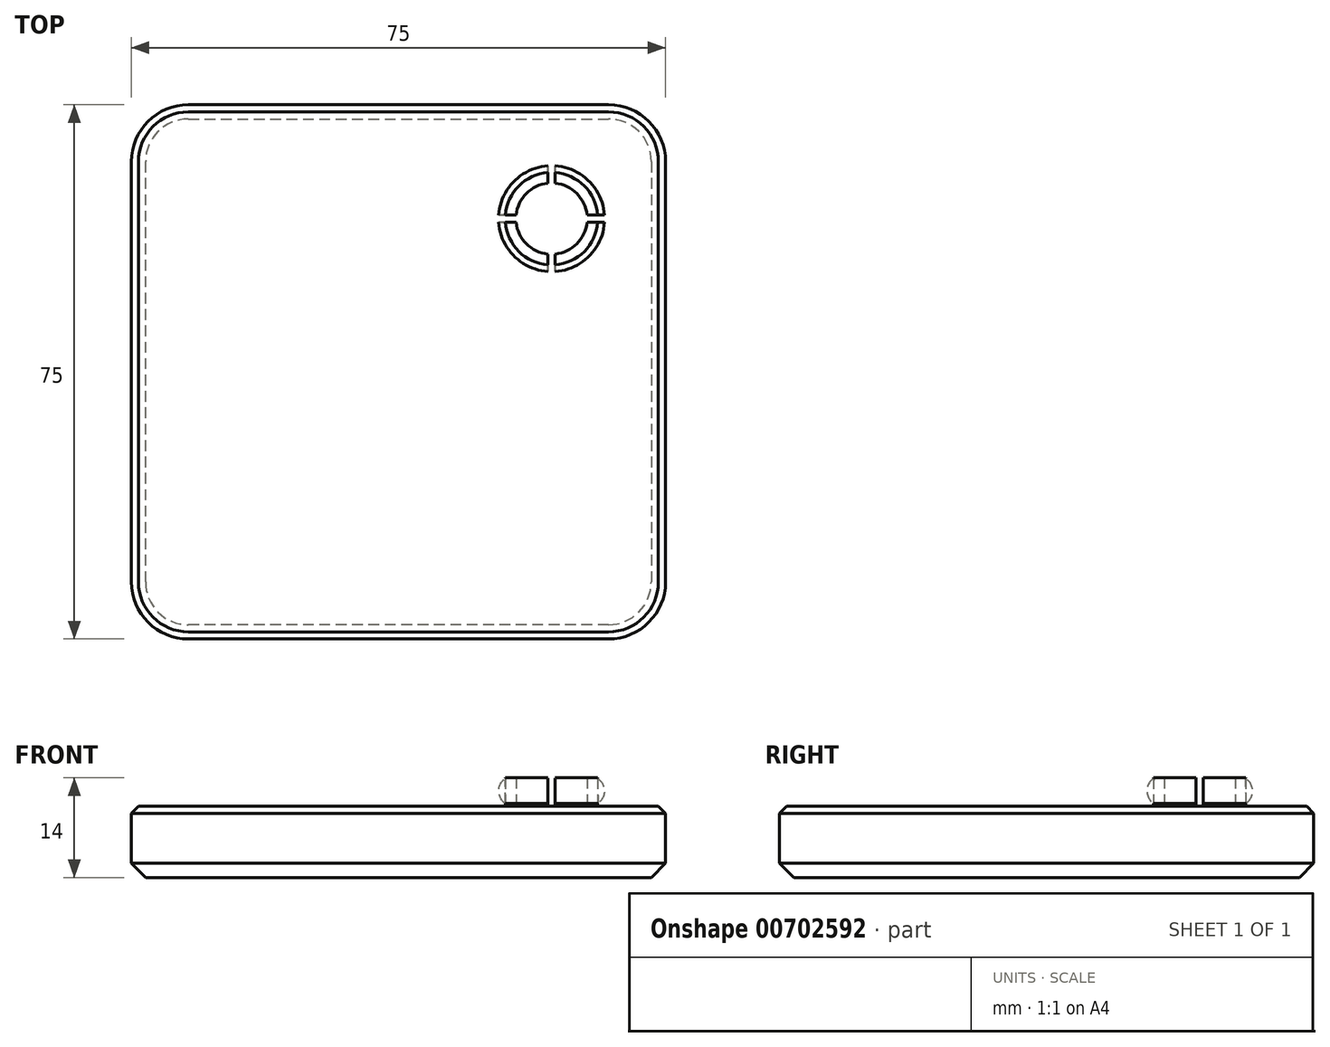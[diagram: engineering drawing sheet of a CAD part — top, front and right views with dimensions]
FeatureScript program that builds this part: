
annotation { "Feature Type Name" : "Feature", "Feature Type Description" : "" }
export const myFeature = defineFeature(function(context is Context, id is Id, definition is map)
    precondition{}
    {
        {
            var Q0;
            Q0=qCreatedBy(makeId("Top.planeOp"),FACE);
            var sketch = newSketch(context, id + "F0", { "sketchPlane" : qUnion([Q0])});
            skLineSegment(sketch, "E0.bottom", {"start": v(16, 16) * mm, "end": v(-59, 16) * mm});
            skLineSegment(sketch, "E0.top", {"start": v(16, -59) * mm, "end": v(-59, -59) * mm});
            skLineSegment(sketch, "E0.left", {"start": v(16, 16) * mm, "end": v(16, -59) * mm});
            skLineSegment(sketch, "E0.right", {"start": v(-59, 16) * mm, "end": v(-59, -59) * mm});
            skCircle(sketch, "E1", {"center": v(0, 0) * mm, "radius": 6.5 * mm});
            skCircle(sketch, "E2.0", {"center": v(0, 0) * mm, "radius": 5 * mm});
            skSolve(sketch);
        }
        {
            var Q0;
            Q0=makeQuery(id+"F0.imprint","IMPRINT",FACE,{"disambiguationData":[TD([[makeQuery(id+"F0.imprint","IMPRINT",EDGE,{"derivedFrom":sQuery(id+"F0.wireOp",EDGE,"E1")}),1.0]])]});
            var Q1;
            Q1=sQuery(id+"F0.wireOp",EDGE,"E1");
            var Q2;
            Q2=sQuery(id+"F0.wireOp",EDGE,"E2.0");
            extrude(context, id + "F1", {"entities" : qUnion([Q0]), "surfaceEntities" : qUnion([Q1, Q2]), "depth" : 4 * mm, "offsetDistance" : 25 * mm});
        }
        {
            var Q0;
            Q0=makeQuery(id+"F0.imprint","IMPRINT",FACE,{"disambiguationData":[TD([[makeQuery(id+"F0.imprint","IMPRINT",EDGE,{"derivedFrom":sQuery(id+"F0.wireOp",EDGE,"E0.bottom")}),1.0]])]});
            var Q1;
            Q1=makeQuery(id+"F0.imprint","IMPRINT",FACE,{"disambiguationData":[TD([[makeQuery(id+"F0.imprint","IMPRINT",EDGE,{"derivedFrom":sQuery(id+"F0.wireOp",EDGE,"E2.0")}),1.0]])]});
            var Q2;
            Q2=makeQuery(id+"F0.imprint","IMPRINT",FACE,{"disambiguationData":[TD([[makeQuery(id+"F0.imprint","IMPRINT",EDGE,{"derivedFrom":sQuery(id+"F0.wireOp",EDGE,"E1")}),1.0]])]});
            extrude(context, id + "F2", {"entities" : qUnion([Q0, Q1, Q2]), "operationType" : NewBodyOperationType.ADD, "oppositeDirection" : true, "depth" : 10 * mm, "offsetDistance" : 25 * mm});
        }
        {
            var Q0;
            Q0=makeQuery(id+"F2.opExtrude","SWEPT_EDGE",EDGE,{"disambiguationData":[OSD([sQuery(id+"F0.wireOp",EDGE,"E0.top"),sQuery(id+"F0.wireOp",EDGE,"E0.right")])]});
            var Q1;
            Q1=makeQuery(id+"F2.opExtrude","SWEPT_EDGE",EDGE,{"disambiguationData":[OSD([sQuery(id+"F0.wireOp",EDGE,"E0.top"),sQuery(id+"F0.wireOp",EDGE,"E0.left")])]});
            var Q2;
            Q2=makeQuery(id+"F2.opExtrude","SWEPT_EDGE",EDGE,{"disambiguationData":[OSD([sQuery(id+"F0.wireOp",EDGE,"E0.bottom"),sQuery(id+"F0.wireOp",EDGE,"E0.left")])]});
            var Q3;
            Q3=makeQuery(id+"F2.opExtrude","SWEPT_EDGE",EDGE,{"disambiguationData":[OSD([sQuery(id+"F0.wireOp",EDGE,"E0.bottom"),sQuery(id+"F0.wireOp",EDGE,"E0.right")])]});
            fillet(context, id + "F3", {"entities" : qUnion([Q0, Q1, Q2, Q3]), "radius" : 8 * mm, "tangentPropagation" : true, "allowEdgeOverflow" : false});
        }
        {
            var Q0;
            Q0=makeQuery(id+"F2.opExtrude","CAP_EDGE",EDGE,{"disambiguationData":[OSD([sQuery(id+"F0.wireOp",EDGE,"E0.top")])],"isStart":false});
            chamfer(context, id + "F4", {"entities" : qUnion([Q0]), "width" : 2 * mm, "tangentPropagation" : true});
        }
        {
            var Q0;
            Q0=makeQuery(id+"F2.opExtrude","CAP_EDGE",EDGE,{"disambiguationData":[OSD([sQuery(id+"F0.wireOp",EDGE,"E0.left")])],"isStart":true});
            chamfer(context, id + "F5", {"entities" : qUnion([Q0]), "width" : 1 * mm, "tangentPropagation" : true});
        }
        {
            var Q0;
            Q0=qCreatedBy(makeId("Front.planeOp"),FACE);
            var sketch = newSketch(context, id + "F6", { "sketchPlane" : qUnion([Q0])});
            skArc(sketch, "E3", {"start": v(6.53, 0.43) * mm, "mid": v(7.44, 2.21) * mm, "end": v(6.47, 3.96) * mm});
            skLineSegment(sketch, "E4", {"start": v(6.53, 0.43) * mm, "end": v(6.47, 3.96) * mm});
            skLineSegment(sketch, "E5", {"start": v(0, 0) * mm, "end": v(0, 0.9) * mm, "construction": true});
            skLineSegment(sketch, "E6", {"start": v(0, 0) * mm, "end": v(0, 16.76) * mm, "construction": true});
            skSolve(sketch);
        }
        {
            var Q0;
            Q0 = qSketchRegion(id + "F6", true);
            var Q1;
            Q1=sQuery(id+"F6.wireOp",EDGE,"E6");
            revolve(context, id + "F7", {"surfaceOperationType" : NewSurfaceOperationType.NEW, "entities" : qUnion([Q0]), "axis" : qUnion([Q1]), "revolveType" : RevolveType.FULL});
        }
        {
            var Q0;
            Q0=makeQuery(id+"F1.opExtrude","CAP_FACE",FACE,{"disambiguationData":[OSD([sQuery(id+"F0.wireOp",EDGE,"E1"),sQuery(id+"F0.wireOp",EDGE,"E2.0")])],"isStart":false});
            var sketch = newSketch(context, id + "F8", { "sketchPlane" : qUnion([Q0])});
            skLineSegment(sketch, "E7.bottom", {"start": v(-9, 0.5) * mm, "end": v(9, 0.5) * mm});
            skLineSegment(sketch, "E7.top", {"start": v(-9, -0.5) * mm, "end": v(9, -0.5) * mm});
            skLineSegment(sketch, "E7.left", {"start": v(-9, 0.5) * mm, "end": v(-9, -0.5) * mm});
            skLineSegment(sketch, "E7.right", {"start": v(9, 0.5) * mm, "end": v(9, -0.5) * mm});
            skPoint(sketch, "E7.middle", {"position": v(0, 0) * mm});
            skLineSegment(sketch, "E8.bottom", {"start": v(-0.5, 9) * mm, "end": v(0.5, 9) * mm});
            skLineSegment(sketch, "E8.top", {"start": v(-0.5, -9) * mm, "end": v(0.5, -9) * mm});
            skLineSegment(sketch, "E8.left", {"start": v(-0.5, 9) * mm, "end": v(-0.5, -9) * mm});
            skLineSegment(sketch, "E8.right", {"start": v(0.5, 9) * mm, "end": v(0.5, -9) * mm});
            skSolve(sketch);
        }
        {
            var Q0;
            {var subQ0=sQuery(id+"F8.wireOp",EDGE,"E7.left");Q0=makeQuery(id+"F8.imprint","IMPRINT",FACE,{"disambiguationData":[TD([[makeQuery(id+"F8.imprint","IMPRINT",EDGE,{"derivedFrom":subQ0}),1.0]])]});}
            var Q1;
            {var subQ0=sQuery(id+"F8.wireOp",EDGE,"E7.bottom");var subQ1=makeQuery(id+"F1.opExtrude","CAP_EDGE",EDGE,{"disambiguationData":[OSD([sQuery(id+"F0.wireOp",EDGE,"E1")])],"isStart":false});var subQ2=makeQuery(id+"F8.imprint","INTERSECT",VERTEX,{"disambiguationData":[OD(0.0)],"derivedFrom":[subQ1,subQ0]});Q1=makeQuery(id+"F8.imprint","IMPRINT",FACE,{"disambiguationData":[TD([[makeQuery(id+"F8.imprint","IMPRINT",EDGE,{"disambiguationData":[TD([[subQ2,-1.0]])],"derivedFrom":subQ0}),-1.0]])]});}
            var Q2;
            {var subQ0=sQuery(id+"F8.wireOp",EDGE,"E8.left");var subQ1=sQuery(id+"F8.wireOp",EDGE,"E7.bottom");var subQ2=makeQuery(id+"F8.imprint","INTERSECT",VERTEX,{"derivedFrom":[subQ1,subQ0]});Q2=makeQuery(id+"F8.imprint","IMPRINT",FACE,{"disambiguationData":[TD([[makeQuery(id+"F8.imprint","IMPRINT",EDGE,{"disambiguationData":[TD([[subQ2,1.0]])],"derivedFrom":subQ1}),-1.0]])]});}
            var Q3;
            {var subQ0=sQuery(id+"F8.wireOp",EDGE,"E8.right");var subQ1=sQuery(id+"F8.wireOp",EDGE,"E7.bottom");var subQ2=makeQuery(id+"F8.imprint","INTERSECT",VERTEX,{"derivedFrom":[subQ1,subQ0]});Q3=makeQuery(id+"F8.imprint","IMPRINT",FACE,{"disambiguationData":[TD([[makeQuery(id+"F8.imprint","IMPRINT",EDGE,{"disambiguationData":[TD([[subQ2,-1.0]])],"derivedFrom":subQ1}),-1.0]])]});}
            var Q4;
            {var subQ0=sQuery(id+"F8.wireOp",EDGE,"E7.bottom");var subQ1=makeQuery(id+"F1.opExtrude","CAP_EDGE",EDGE,{"disambiguationData":[OSD([sQuery(id+"F0.wireOp",EDGE,"E1")])],"isStart":false});var subQ2=makeQuery(id+"F8.imprint","INTERSECT",VERTEX,{"disambiguationData":[OD(1.0)],"derivedFrom":[subQ1,subQ0]});Q4=makeQuery(id+"F8.imprint","IMPRINT",FACE,{"disambiguationData":[TD([[makeQuery(id+"F8.imprint","IMPRINT",EDGE,{"disambiguationData":[TD([[subQ2,1.0]])],"derivedFrom":subQ0}),-1.0]])]});}
            var Q5;
            {var subQ0=sQuery(id+"F8.wireOp",EDGE,"E7.right");Q5=makeQuery(id+"F8.imprint","IMPRINT",FACE,{"disambiguationData":[TD([[makeQuery(id+"F8.imprint","IMPRINT",EDGE,{"derivedFrom":subQ0}),-1.0]])]});}
            var Q6;
            {var subQ0=sQuery(id+"F8.wireOp",EDGE,"E8.left");var subQ1=sQuery(id+"F8.wireOp",EDGE,"E7.bottom");var subQ2=makeQuery(id+"F8.imprint","INTERSECT",VERTEX,{"derivedFrom":[subQ1,subQ0]});Q6=makeQuery(id+"F8.imprint","IMPRINT",FACE,{"disambiguationData":[TD([[makeQuery(id+"F8.imprint","IMPRINT",EDGE,{"disambiguationData":[TD([[subQ2,-1.0]])],"derivedFrom":subQ1}),1.0]])]});}
            var Q7;
            {var subQ0=sQuery(id+"F8.wireOp",EDGE,"E8.left");var subQ1=makeQuery(id+"F1.opExtrude","CAP_EDGE",EDGE,{"disambiguationData":[OSD([sQuery(id+"F0.wireOp",EDGE,"E1")])],"isStart":false});var subQ2=makeQuery(id+"F8.imprint","INTERSECT",VERTEX,{"disambiguationData":[OD(0.0)],"derivedFrom":[subQ1,subQ0]});Q7=makeQuery(id+"F8.imprint","IMPRINT",FACE,{"disambiguationData":[TD([[makeQuery(id+"F8.imprint","IMPRINT",EDGE,{"disambiguationData":[TD([[subQ2,-1.0]])],"derivedFrom":subQ0}),1.0]])]});}
            var Q8;
            {var subQ0=sQuery(id+"F8.wireOp",EDGE,"E8.bottom");Q8=makeQuery(id+"F8.imprint","IMPRINT",FACE,{"disambiguationData":[TD([[makeQuery(id+"F8.imprint","IMPRINT",EDGE,{"derivedFrom":subQ0}),-1.0]])]});}
            var Q9;
            {var subQ0=sQuery(id+"F8.wireOp",EDGE,"E8.left");var subQ1=sQuery(id+"F8.wireOp",EDGE,"E7.top");var subQ2=makeQuery(id+"F8.imprint","INTERSECT",VERTEX,{"derivedFrom":[subQ1,subQ0]});Q9=makeQuery(id+"F8.imprint","IMPRINT",FACE,{"disambiguationData":[TD([[makeQuery(id+"F8.imprint","IMPRINT",EDGE,{"disambiguationData":[TD([[subQ2,-1.0]])],"derivedFrom":subQ1}),-1.0]])]});}
            var Q10;
            {var subQ0=sQuery(id+"F8.wireOp",EDGE,"E8.left");var subQ1=makeQuery(id+"F1.opExtrude","CAP_EDGE",EDGE,{"disambiguationData":[OSD([sQuery(id+"F0.wireOp",EDGE,"E1")])],"isStart":false});var subQ2=makeQuery(id+"F8.imprint","INTERSECT",VERTEX,{"disambiguationData":[OD(1.0)],"derivedFrom":[subQ1,subQ0]});Q10=makeQuery(id+"F8.imprint","IMPRINT",FACE,{"disambiguationData":[TD([[makeQuery(id+"F8.imprint","IMPRINT",EDGE,{"disambiguationData":[TD([[subQ2,1.0]])],"derivedFrom":subQ0}),1.0]])]});}
            var Q11;
            {var subQ0=sQuery(id+"F8.wireOp",EDGE,"E8.top");Q11=makeQuery(id+"F8.imprint","IMPRINT",FACE,{"disambiguationData":[TD([[makeQuery(id+"F8.imprint","IMPRINT",EDGE,{"derivedFrom":subQ0}),1.0]])]});}
            extrude(context, id + "F9", {"entities" : qUnion([Q0, Q1, Q2, Q3, Q4, Q5, Q6, Q7, Q8, Q9, Q10, Q11]), "operationType" : NewBodyOperationType.REMOVE, "oppositeDirection" : true, "depth" : 4 * mm, "offsetDistance" : 25 * mm});
        }
    });
